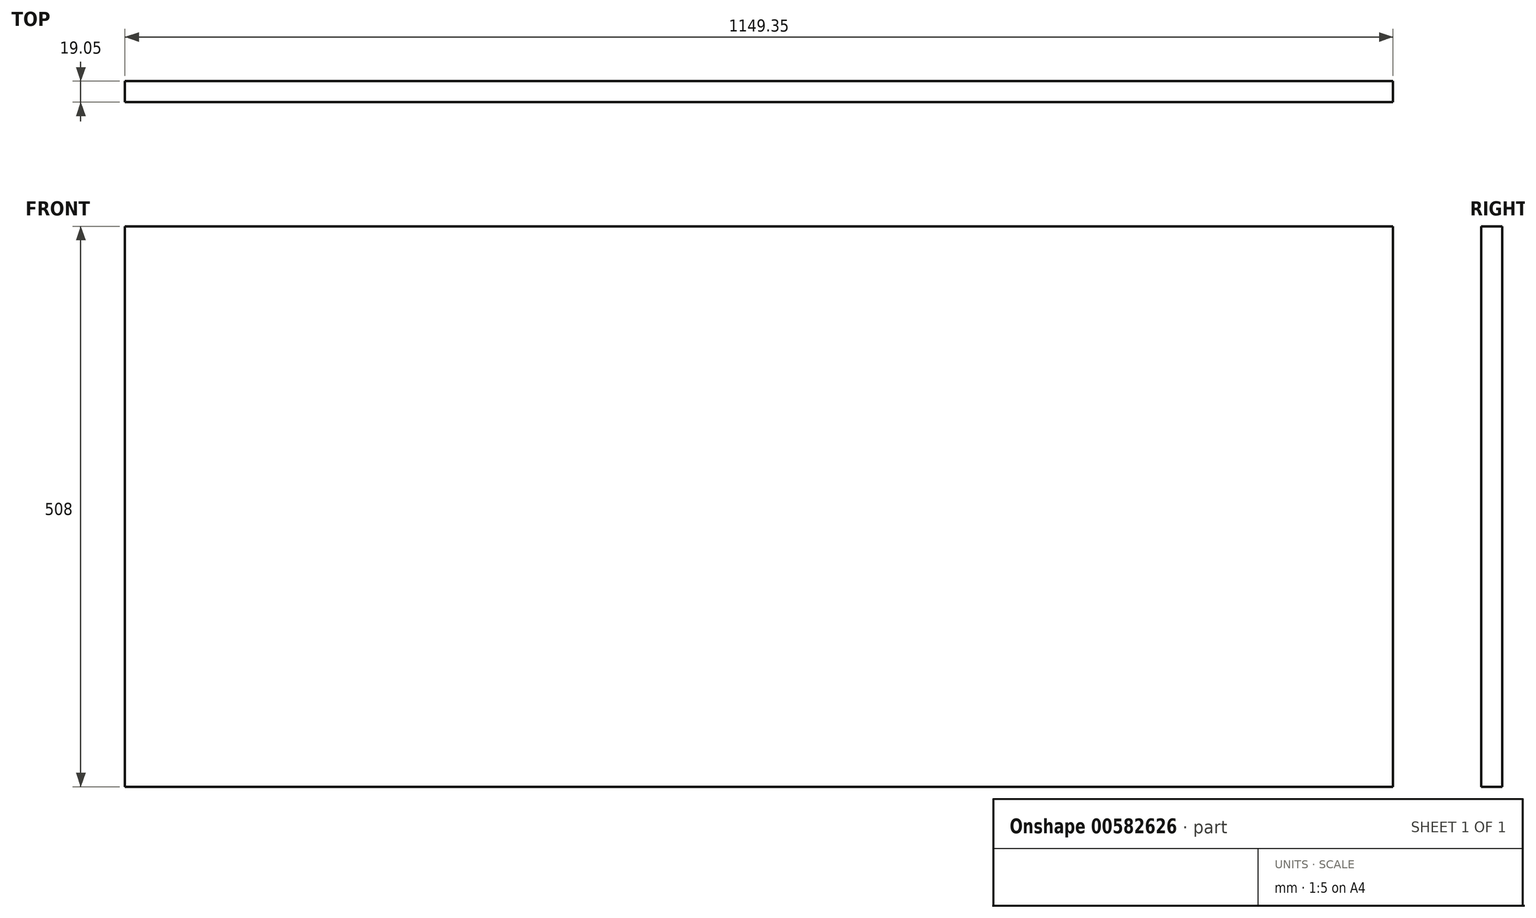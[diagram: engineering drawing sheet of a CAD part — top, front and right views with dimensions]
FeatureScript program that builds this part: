
annotation { "Feature Type Name" : "Feature", "Feature Type Description" : "" }
export const myFeature = defineFeature(function(context is Context, id is Id, definition is map)
    precondition{}
    {
        {
            var Q0;
            Q0=qCreatedBy(makeId("Top.planeOp"),FACE);
            var sketch = newSketch(context, id + "F0", { "sketchPlane" : qUnion([Q0])});
            skLineSegment(sketch, "E0.bottom", {"start": v(892.56, 56.07) * mm, "end": v(-256.79, 56.07) * mm});
            skLineSegment(sketch, "E0.top", {"start": v(892.56, 75.12) * mm, "end": v(-256.79, 75.12) * mm});
            skLineSegment(sketch, "E0.left", {"start": v(892.56, 56.07) * mm, "end": v(892.56, 75.12) * mm});
            skLineSegment(sketch, "E0.right", {"start": v(-256.79, 56.07) * mm, "end": v(-256.79, 75.12) * mm});
            skPoint(sketch, "E0.middle", {"position": v(317.89, 65.6) * mm});
            skSolve(sketch);
        }
        {
            var Q0;
            Q0=qSketchRegion(id+"F0",true);
            extrude(context, id + "F1", {"entities" : qUnion([Q0]), "depth" : 508 * mm, "offsetDistance" : 25.4 * mm});
        }
    });
